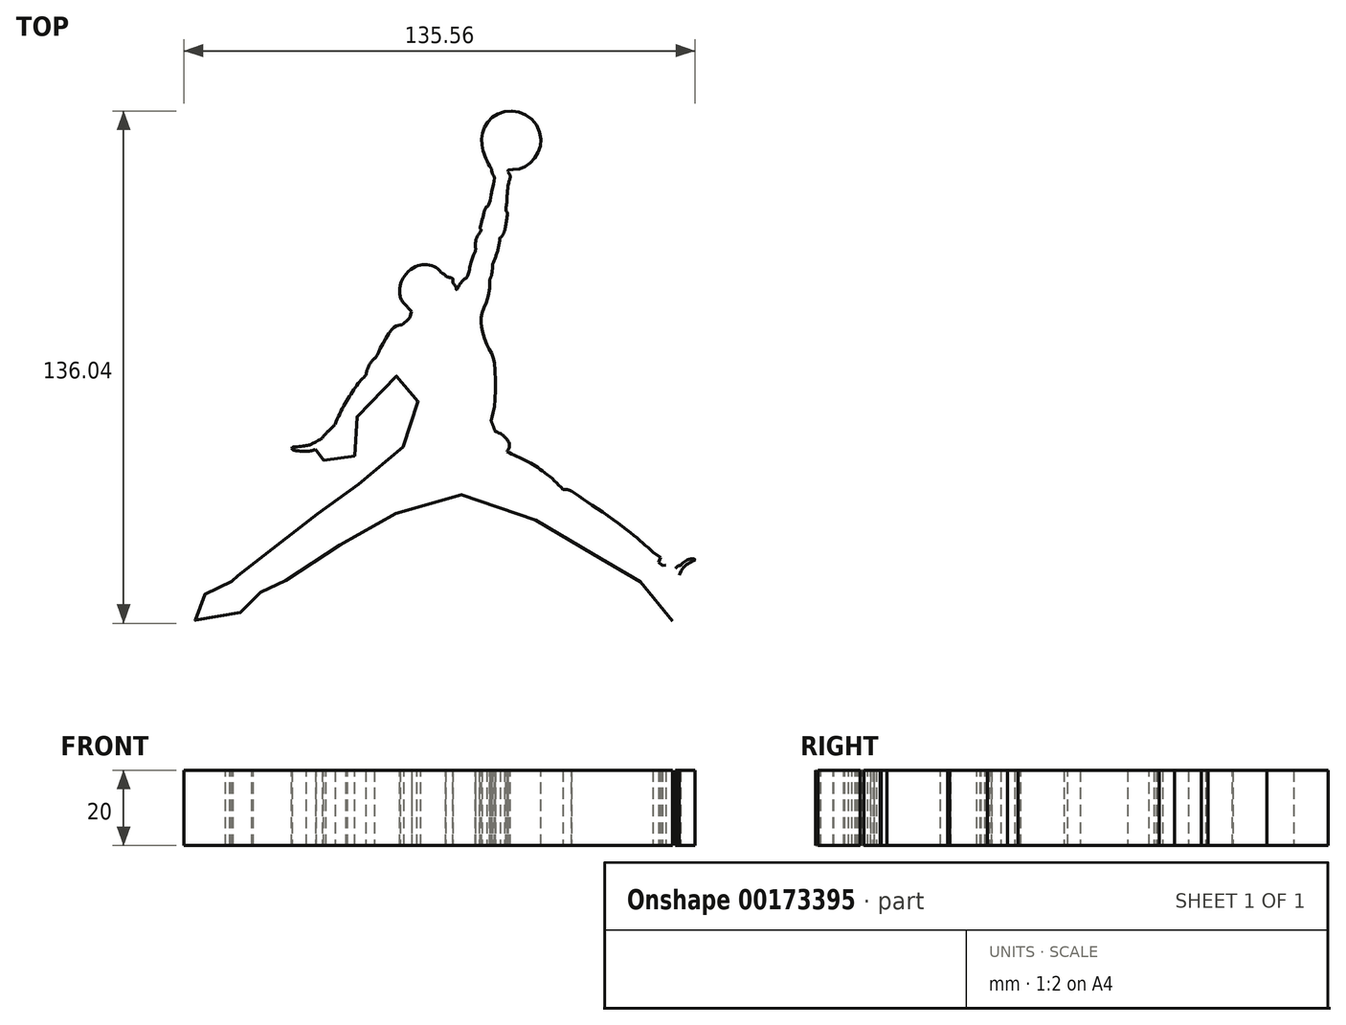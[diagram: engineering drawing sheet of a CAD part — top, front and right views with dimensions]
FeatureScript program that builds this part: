
annotation { "Feature Type Name" : "Feature", "Feature Type Description" : "" }
export const myFeature = defineFeature(function(context is Context, id is Id, definition is map)
    precondition{}
    {
        {
            var Q0;
            Q0=qCreatedBy(makeId("Top.planeOp"),FACE);
            var sketch = newSketch(context, id + "F0", { "sketchPlane" : qUnion([Q0])});
            skFitSpline(sketch, "E0", {"points": [v(56.89, -67.5) * mm, v(58.77, -66.21) * mm, v(60.28, -64.81) * mm, v(62.6, -63.1) * mm, v(65.53, -61.44) * mm, v(69.3, -58.45) * mm, v(72.83, -54.98) * mm, v(72.99, -54.68) * mm, v(72.86, -54.15) * mm, v(71.61, -53.22) * mm, v(69.54, -53.33) * mm, v(66.84, -55.06) * mm, v(60.54, -55.26) * mm, v(58.7, -55.32) * mm, v(58.7, -55.32) * mm], "startDerivative": vector(28.95, 13.7) * mm, "endDerivative": vector(4.42, 3.17) * mm});
            skFitSpline(sketch, "E1", {"points": [v(58.7, -55.32) * mm, v(60.72, -52.43) * mm, v(62.8, -51.32) * mm, v(62.7, -51.1) * mm, v(60.99, -51.22) * mm, v(59.01, -52.75) * mm], "startDerivative": vector(5.84, 13.08) * mm, "endDerivative": vector(-7.98, -7.84) * mm});
            skLineSegment(sketch, "E2", {"start": v(59.01, -52.75) * mm, "end": v(58.4, -52.75) * mm});
            skLineSegment(sketch, "E3", {"start": v(58.4, -52.75) * mm, "end": v(57.7, -53.5) * mm});
            skFitSpline(sketch, "E4", {"points": [v(57.7, -53.5) * mm, v(56.38, -53.61) * mm, v(55.18, -52.66) * mm, v(55.18, -52.66) * mm], "startDerivative": vector(-1.52, -1.11) * mm, "endDerivative": vector(0.35, 1.09) * mm});
            skLineSegment(sketch, "E5", {"start": v(55.18, -52.66) * mm, "end": v(54.27, -52.79) * mm});
            skLineSegment(sketch, "E6", {"start": v(54.27, -52.79) * mm, "end": v(53.17, -51.94) * mm});
            skLineSegment(sketch, "E7", {"start": v(53.17, -51.94) * mm, "end": v(53.68, -50.62) * mm});
            skLineSegment(sketch, "E8", {"start": v(53.68, -50.62) * mm, "end": v(51.63, -49.21) * mm});
            skFitSpline(sketch, "E9", {"points": [v(51.63, -49.21) * mm, v(43.38, -42.22) * mm, v(30.08, -33.02) * mm, v(30.07, -33.02) * mm], "startDerivative": vector(-14.36, 13.49) * mm, "endDerivative": vector(1.99, -2.64) * mm});
            skFitSpline(sketch, "E10", {"points": [v(30.06, -33) * mm, v(29.05, -32.65) * mm, v(27.82, -32.54) * mm], "startDerivative": vector(-2.1, 0.96) * mm, "endDerivative": vector(-2.47, 0.07) * mm});
            skFitSpline(sketch, "E11", {"points": [v(27.82, -32.54) * mm, v(25.16, -29.88) * mm, v(22.07, -27.44) * mm, v(19.46, -25.74) * mm, v(15.8, -23.9) * mm, v(12.95, -22.53) * mm], "startDerivative": vector(-12.49, 13.12) * mm, "endDerivative": vector(-14.5, 7.38) * mm});
            skFitSpline(sketch, "E12", {"points": [v(12.95, -22.53) * mm, v(13.4, -21.87) * mm, v(13.58, -20.44) * mm, v(12.63, -18.91) * mm, v(11.5, -17.94) * mm, v(9.87, -17.16) * mm, v(9.84, -17.16) * mm], "startDerivative": vector(3.35, 3.93) * mm, "endDerivative": vector(-0.61, -0.21) * mm});
            skFitSpline(sketch, "E13", {"points": [v(9.85, -17.16) * mm, v(8.72, -14.36) * mm], "startDerivative": vector(-1.1, 2.8) * mm, "endDerivative": vector(-1.45, 2.66) * mm});
            skFitSpline(sketch, "E14", {"points": [v(8.72, -14.36) * mm, v(9.21, -12.61) * mm, v(9.85, -8.33) * mm, v(9.67, 0.54) * mm, v(8.97, 3.42) * mm, v(7.78, 5.41) * mm, v(6.42, 9.57) * mm, v(6.12, 11.74) * mm, v(6.36, 14.13) * mm, v(7.54, 17.23) * mm, v(8.34, 23.04) * mm], "startDerivative": vector(6.78, 22.75) * mm, "endDerivative": vector(-7.96, 49.58) * mm});
            skFitSpline(sketch, "E15", {"points": [v(8.34, 23.04) * mm, v(8.93, 24.58) * mm, v(9.15, 27.15) * mm], "startDerivative": vector(1.86, 3.1) * mm, "endDerivative": vector(0.06, 5.02) * mm});
            skFitSpline(sketch, "E16", {"points": [v(9.15, 27.15) * mm, v(10.45, 30.64) * mm, v(11.16, 34.3) * mm], "startDerivative": vector(2.89, 6.88) * mm, "endDerivative": vector(1.13, 7.42) * mm});
            skFitSpline(sketch, "E17", {"points": [v(11.16, 34.3) * mm, v(11.7, 34.75) * mm, v(12.36, 36.1) * mm], "startDerivative": vector(1.4, 0.84) * mm, "endDerivative": vector(1.02, 2.61) * mm});
            skFitSpline(sketch, "E18", {"points": [v(12.36, 36.08) * mm, v(12.77, 38.47) * mm, v(12.97, 41.07) * mm, v(12.67, 41.44) * mm, v(12.85, 43.03) * mm], "startDerivative": vector(1.54, 6.84) * mm, "endDerivative": vector(0.5, 6) * mm});
            skFitSpline(sketch, "E19", {"points": [v(12.85, 43.03) * mm, v(13.34, 48.4) * mm, v(13.8, 50.32) * mm, v(13.26, 51.7) * mm], "startDerivative": vector(1.12, 14.3) * mm, "endDerivative": vector(-6.7, 7.92) * mm});
            skFitSpline(sketch, "E20", {"points": [v(13.26, 51.7) * mm, v(13.26, 52.04) * mm, v(13.47, 52.29) * mm, v(15.48, 52.4) * mm, v(17.95, 53.2) * mm, v(20.04, 55) * mm, v(21.55, 57.73) * mm, v(21.94, 60.7) * mm, v(20.84, 64.17) * mm, v(18.05, 66.84) * mm, v(14.76, 67.88) * mm, v(11.22, 67.37) * mm, v(8.64, 65.8) * mm, v(7, 63.6) * mm, v(6.34, 61.24) * mm, v(6.41, 58.81) * mm], "startDerivative": vector(-1.31, 14.34) * mm, "endDerivative": vector(7.43, -40.2) * mm});
            skFitSpline(sketch, "E21", {"points": [v(6.41, 58.81) * mm, v(6.84, 56.72) * mm, v(7.68, 54.71) * mm, v(8.5, 53.09) * mm, v(8.96, 52.33) * mm, v(8.98, 51.5) * mm, v(9.52, 50.45) * mm, v(9.29, 48.11) * mm, v(7.94, 42.55) * mm, v(7.66, 42.6) * mm], "startDerivative": vector(2.57, -17.3) * mm, "endDerivative": vector(-7.97, 1.2) * mm});
            skFitSpline(sketch, "E22", {"points": [v(7.66, 42.6) * mm, v(7.39, 42.35) * mm, v(5.91, 37.1) * mm, v(5.86, 36.62) * mm, v(6.1, 36.43) * mm, v(5.57, 35.38) * mm], "startDerivative": vector(-2.29, -0.74) * mm, "endDerivative": vector(-6.8, -9.98) * mm});
            skFitSpline(sketch, "E23", {"points": [v(5.57, 35.38) * mm, v(4.66, 33.21) * mm, v(4.65, 31.24) * mm, v(4.6, 30.87) * mm], "startDerivative": vector(-2.55, -4.35) * mm, "endDerivative": vector(-0.47, -0.43) * mm});
            skFitSpline(sketch, "E24", {"points": [v(4.63, 30.9) * mm, v(3.64, 28.3) * mm, v(2.38, 23.78) * mm, v(2.12, 23.5) * mm], "startDerivative": vector(-2.56, -5.65) * mm, "endDerivative": vector(-1.73, -1.02) * mm});
            skFitSpline(sketch, "E25", {"points": [v(2.12, 23.5) * mm, v(0.77, 22.33) * mm, v(-0.44, 20.45) * mm, v(-0.55, 21.04) * mm, v(-1.3, 22.15) * mm, v(-1.38, 22.3) * mm], "startDerivative": vector(-5.24, -3.1) * mm, "endDerivative": vector(0.3, 1.69) * mm});
            skFitSpline(sketch, "E26", {"points": [v(-1.38, 22.3) * mm, v(-1.38, 23.27) * mm, v(-1.38, 23.34) * mm, v(-2.28, 23.7) * mm, v(-3.3, 24.03) * mm], "startDerivative": vector(0, 4.16) * mm, "endDerivative": vector(0.24, 0.95) * mm});
            skFitSpline(sketch, "E27", {"points": [v(-3.3, 24.03) * mm, v(-3.37, 24.24) * mm, v(-3.77, 24.6) * mm, v(-4.35, 24.88) * mm, v(-4.94, 25.52) * mm, v(-5.93, 26.34) * mm, v(-7.01, 26.82) * mm, v(-8.45, 27.13) * mm, v(-9.57, 27.07) * mm, v(-10.52, 26.87) * mm, v(-11.93, 26.24) * mm, v(-13.66, 24.81) * mm, v(-15.34, 21.66) * mm], "startDerivative": vector(-0.07, 7.87) * mm, "endDerivative": vector(-1.4, -17.76) * mm});
            skFitSpline(sketch, "E28", {"points": [v(-15.34, 21.66) * mm, v(-15.52, 19.58) * mm, v(-14.96, 17.64) * mm, v(-13.65, 16.01) * mm, v(-12.3, 14.66) * mm], "startDerivative": vector(-1.3, -8.24) * mm, "endDerivative": vector(6.01, -4.9) * mm});
            skFitSpline(sketch, "E29", {"points": [v(-12.3, 14.66) * mm, v(-12.44, 14.44) * mm, v(-12.79, 13.3) * mm, v(-13.38, 12.46) * mm, v(-14.46, 11.47) * mm, v(-15.04, 11.09) * mm, v(-15.9, 11) * mm, v(-17.67, 9.8) * mm, v(-21.22, 3.65) * mm, v(-21.77, 2.56) * mm, v(-22.24, 2.14) * mm], "startDerivative": vector(-5.87, -4.28) * mm, "endDerivative": vector(-5.22, -3.65) * mm});
            skFitSpline(sketch, "E30", {"points": [v(-22.24, 2.14) * mm, v(-22.99, 1.32) * mm, v(-23.96, -0.4) * mm, v(-24.47, -2.23) * mm], "startDerivative": vector(-2.67, -2.6) * mm, "endDerivative": vector(-1.13, -5.05) * mm});
            skFitSpline(sketch, "E31", {"points": [v(-24.47, -2.23) * mm, v(-25.74, -3.54) * mm, v(-28.02, -6.58) * mm, v(-30.4, -10.53) * mm, v(-32.69, -15.3) * mm], "startDerivative": vector(-6.8, -6.58) * mm, "endDerivative": vector(-6.85, -15.67) * mm});
            skFitSpline(sketch, "E32", {"points": [v(-32.69, -15.3) * mm, v(-33.94, -16.64) * mm, v(-34.89, -17.55) * mm, v(-36.05, -18.95) * mm], "startDerivative": vector(-4.22, -4.79) * mm, "endDerivative": vector(-2.94, -4.79) * mm});
            skFitSpline(sketch, "E33", {"points": [v(-36.05, -18.95) * mm, v(-38.23, -20.24) * mm, v(-39.28, -20.7) * mm, v(-41.4, -21.11) * mm, v(-44.06, -21.36) * mm], "startDerivative": vector(-7, -4) * mm, "endDerivative": vector(-0.67, 0.28) * mm});
            skFitSpline(sketch, "E34", {"points": [v(-44.06, -21.36) * mm, v(-44.08, -21.9) * mm, v(-42.76, -22.29) * mm, v(-39.54, -22.4) * mm, v(-37.8, -21.93) * mm], "startDerivative": vector(-1.9, -3.88) * mm, "endDerivative": vector(4.18, 1.96) * mm});
            skFitSpline(sketch, "E35", {"points": [v(-37.8, -21.93) * mm, v(-37.55, -22.1) * mm, v(-39.88, -23.54) * mm, v(-40.2, -23.96) * mm, v(-39.65, -24.34) * mm, v(-36.58, -23.65) * mm, v(-35.68, -23.3) * mm, v(-35.38, -23.19) * mm, v(-35.06, -23.24) * mm, v(-35.33, -24.03) * mm, v(-35.62, -24.66) * mm, v(-35.57, -25.26) * mm, v(-34.24, -25.04) * mm, v(-33.35, -23.9) * mm, v(-32.56, -22.9) * mm, v(-31.88, -22.57) * mm, v(-31.08, -23.05) * mm, v(-30.34, -23.82) * mm, v(-28.7, -24.07) * mm, v(-27.67, -23.96) * mm, v(-27.48, -23.1) * mm, v(-28.8, -22.57) * mm, v(-29.54, -21.84) * mm, v(-29.6, -21.3) * mm, v(-29.32, -20.64) * mm, v(-29.56, -19.97) * mm, v(-29.56, -18.56) * mm, v(-28.24, -15.51) * mm, v(-26.5, -12.87) * mm, v(-26.34, -12.76) * mm, v(-22.38, -10) * mm, v(-19.41, -6.23) * mm, v(-18.51, -4.33) * mm, v(-18.08, -3.37) * mm, v(-17.32, -3.16) * mm, v(-16.03, -2.1) * mm, v(-15.77, -1.36) * mm, v(-14.56, -1.3) * mm, v(-13.75, -2.62) * mm, v(-12.17, -4.8) * mm, v(-12.23, -5.14) * mm, v(-11.87, -6.4) * mm, v(-10.87, -7.57) * mm, v(-10.9, -8.06) * mm, v(-9.88, -11.53) * mm, v(-10, -11.76) * mm, v(-11.41, -13.56) * mm, v(-11.77, -13.61) * mm, v(-13.28, -14.28) * mm, v(-14.32, -17.13) * mm, v(-14.34, -20.62) * mm, v(-14.72, -21.35) * mm, v(-16.07, -22.57) * mm, v(-16.64, -22.67) * mm, v(-17.7, -22.94) * mm, v(-18.64, -23.86) * mm, v(-19.02, -24.63) * mm, v(-19.44, -24.9) * mm, v(-24.16, -28.87) * mm, v(-28.54, -34.12) * mm, v(-28.99, -34.86) * mm, v(-29.8, -34.91) * mm, v(-31.55, -35.53) * mm, v(-33.2, -36.95) * mm, v(-33.5, -37.33) * mm, v(-33.88, -37.5) * mm, v(-37.25, -39.06) * mm, v(-43.62, -42.63) * mm, v(-47.4, -45.53) * mm, v(-51.12, -48.9) * mm, v(-53.07, -51.1) * mm, v(-54.33, -52.16) * mm, v(-54.68, -52.45) * mm, v(-54.61, -52.98) * mm, v(-54.39, -53.28) * mm, v(-54.57, -53.51) * mm, v(-54.94, -53.75) * mm, v(-55.37, -54.17) * mm, v(-55.83, -54.05) * mm, v(-56.21, -53.54) * mm, v(-56.67, -53.52) * mm, v(-57.13, -53.74) * mm, v(-57.9, -55.14) * mm, v(-58.17, -55.43) * mm, v(-58.83, -55.38) * mm, v(-59.17, -54.35) * mm, v(-59.42, -53.44) * mm, v(-59.74, -52.7) * mm, v(-60.02, -52.45) * mm, v(-60.58, -52.94) * mm, v(-60.2, -54.44) * mm, v(-60.1, -55) * mm, v(-60.13, -55.53) * mm, v(-59.7, -56.57) * mm, v(-60, -57) * mm, v(-60.5, -56.73) * mm, v(-60.87, -56.79) * mm, v(-61.65, -57.5) * mm, v(-61.68, -58.39) * mm, v(-62.03, -58.57) * mm, v(-63.14, -59.27) * mm, v(-64.02, -59.3) * mm, v(-65.54, -59.9) * mm, v(-65.8, -60) * mm, v(-66.43, -60.1) * mm, v(-66.9, -60.35) * mm, v(-67.95, -60.33) * mm, v(-68.62, -60.59) * mm, v(-69.8, -60.66) * mm, v(-71.15, -61.2) * mm, v(-72.56, -62.56) * mm, v(-72.63, -63.94) * mm, v(-71.75, -65.27) * mm, v(-70.14, -66.96) * mm, v(-68.64, -67.86) * mm, v(-66.1, -68.04) * mm, v(-64.35, -67.09) * mm, v(-62.5, -66.66) * mm, v(-60.63, -67.17) * mm, v(-58.97, -66.66) * mm, v(-57.86, -65.43) * mm, v(-57.77, -65) * mm, v(-57.43, -64.88) * mm, v(-57.14, -64.64) * mm, v(-56.75, -63.92) * mm, v(-56.2, -63.36) * mm, v(-55.46, -63.31) * mm, v(-54.78, -62.77) * mm, v(-54, -61.42) * mm, v(-53.42, -60.7) * mm, v(-53.1, -60.36) * mm, v(-52.7, -60.3) * mm, v(-52.43, -60.1) * mm, v(-52.35, -59.62) * mm, v(-51.7, -59.07) * mm, v(-51.07, -58.8) * mm, v(-50.75, -58.44) * mm, v(-50.17, -58.45) * mm, v(-49.63, -58.25) * mm, v(-48.14, -57.2) * mm, v(-48, -57.03) * mm, v(-47.57, -57.33) * mm, v(-46.97, -57.51) * mm, v(-46.4, -57.36) * mm, v(-45.87, -56.86) * mm, v(-44.37, -55.6) * mm, v(-40.46, -52.7) * mm, v(-38.55, -51.28) * mm, v(-37.8, -51.15) * mm, v(-33.52, -48.7) * mm, v(-31.2, -47.2) * mm, v(-28.1, -45.16) * mm, v(-25.54, -43.24) * mm, v(-24.93, -42.7) * mm, v(-24.06, -42.38) * mm, v(-21.73, -41.27) * mm, v(-16.01, -38.66) * mm, v(-10.34, -35.45) * mm, v(-4.14, -32.32) * mm, v(-2.91, -32.28) * mm, v(-1.98, -32.84) * mm, v(0, -33.73) * mm, v(4.1, -34.79) * mm, v(10.16, -37.38) * mm, v(11.34, -37.87) * mm, v(15.81, -39.78) * mm, v(20.9, -40.77) * mm, v(23.78, -41.4) * mm, v(25.54, -42.5) * mm, v(27.29, -43.31) * mm, v(30.3, -45.53) * mm, v(34.86, -48.87) * mm, v(37.73, -51.19) * mm, v(39.3, -51.35) * mm, v(39.97, -51.85) * mm, v(43.58, -54.76) * mm, v(46.11, -56.47) * mm, v(47.37, -56.24) * mm, v(48.96, -57.68) * mm, v(51.15, -59.74) * mm, v(51.85, -60.26) * mm, v(52.43, -61.43) * mm, v(54.39, -63.29) * mm, v(54.54, -63.96) * mm, v(56, -67.07) * mm, v(56.89, -67.5) * mm], "startDerivative": vector(169.47, -48.34) * mm, "endDerivative": vector(184.32, -33.77) * mm});
            skLineSegment(sketch, "E36", {"start": v(9.85, -17.16) * mm, "end": v(9.84, -17.16) * mm});
            skLineSegment(sketch, "E37", {"start": v(30.06, -33) * mm, "end": v(30.07, -33.02) * mm});
            skLineSegment(sketch, "E38", {"start": v(4.6, 30.87) * mm, "end": v(4.63, 30.9) * mm});
            skSolve(sketch);
        }
        {
            var Q0;
            Q0 = qConstructionFilter(qBodyType(qCreatedBy(id + "F0" ,EDGE), BodyType.WIRE), ConstructionObject.NO);
            extrude(context, id + "F1", {"bodyType" : ToolBodyType.SURFACE, "surfaceEntities" : qUnion([Q0]), "oppositeDirection" : true, "depth" : 20 * mm});
        }
    });
